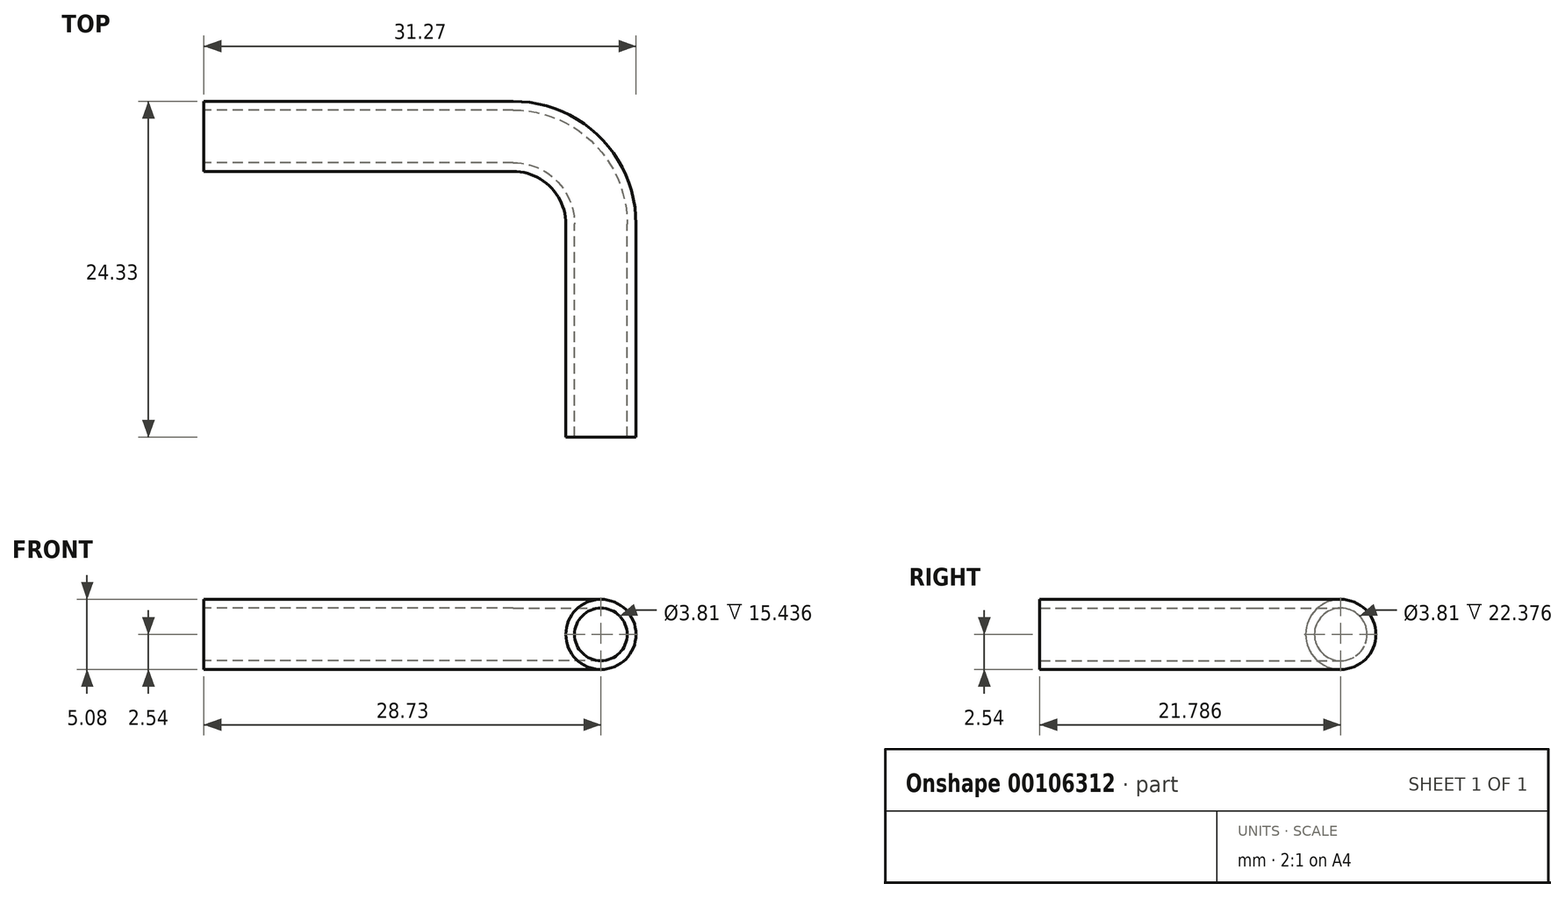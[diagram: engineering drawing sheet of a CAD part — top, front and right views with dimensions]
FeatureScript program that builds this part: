
annotation { "Feature Type Name" : "Feature", "Feature Type Description" : "" }
export const myFeature = defineFeature(function(context is Context, id is Id, definition is map)
    precondition{}
    {
        {
            var Q0;
            Q0=qCreatedBy(makeId("Front.planeOp"),FACE);
            var sketch = newSketch(context, id + "F0", { "sketchPlane" : qUnion([Q0])});
            skCircle(sketch, "E0", {"center": v(0, 0) * mm, "radius": 2.54 * mm});
            skCircle(sketch, "E1", {"center": v(0, 0) * mm, "radius": 1.9 * mm});
            skSolve(sketch);
        }
        {
            var Q0;
            Q0=qCreatedBy(makeId("Top.planeOp"),FACE);
            var sketch = newSketch(context, id + "F1", { "sketchPlane" : qUnion([Q0])});
            skLineSegment(sketch, "E2", {"start": v(0, 0) * mm, "end": v(0, 15.44) * mm});
            skLineSegment(sketch, "E3", {"start": v(-6.35, 21.79) * mm, "end": v(-28.73, 21.79) * mm});
            skPoint(sketch, "E4.visualSharp", {"position": v(0, 21.79) * mm});
            skArc(sketch, "E4.filletArc", {"start": v(0, 15.44) * mm, "mid": v(-1.86, 19.93) * mm, "end": v(-6.35, 21.79) * mm});
            skSolve(sketch);
        }
        {
            var Q0;
            Q0 = qSketchRegion(id + "F0", true);
            var Q1;
            Q1 = qConstructionFilter(qBodyType(qCreatedBy(id + "F1" ,EDGE), BodyType.WIRE), ConstructionObject.NO);
            sweep(context, id + "F2", {"profiles" : qUnion([Q0]), "path" : qUnion([Q1])});
        }
    });
